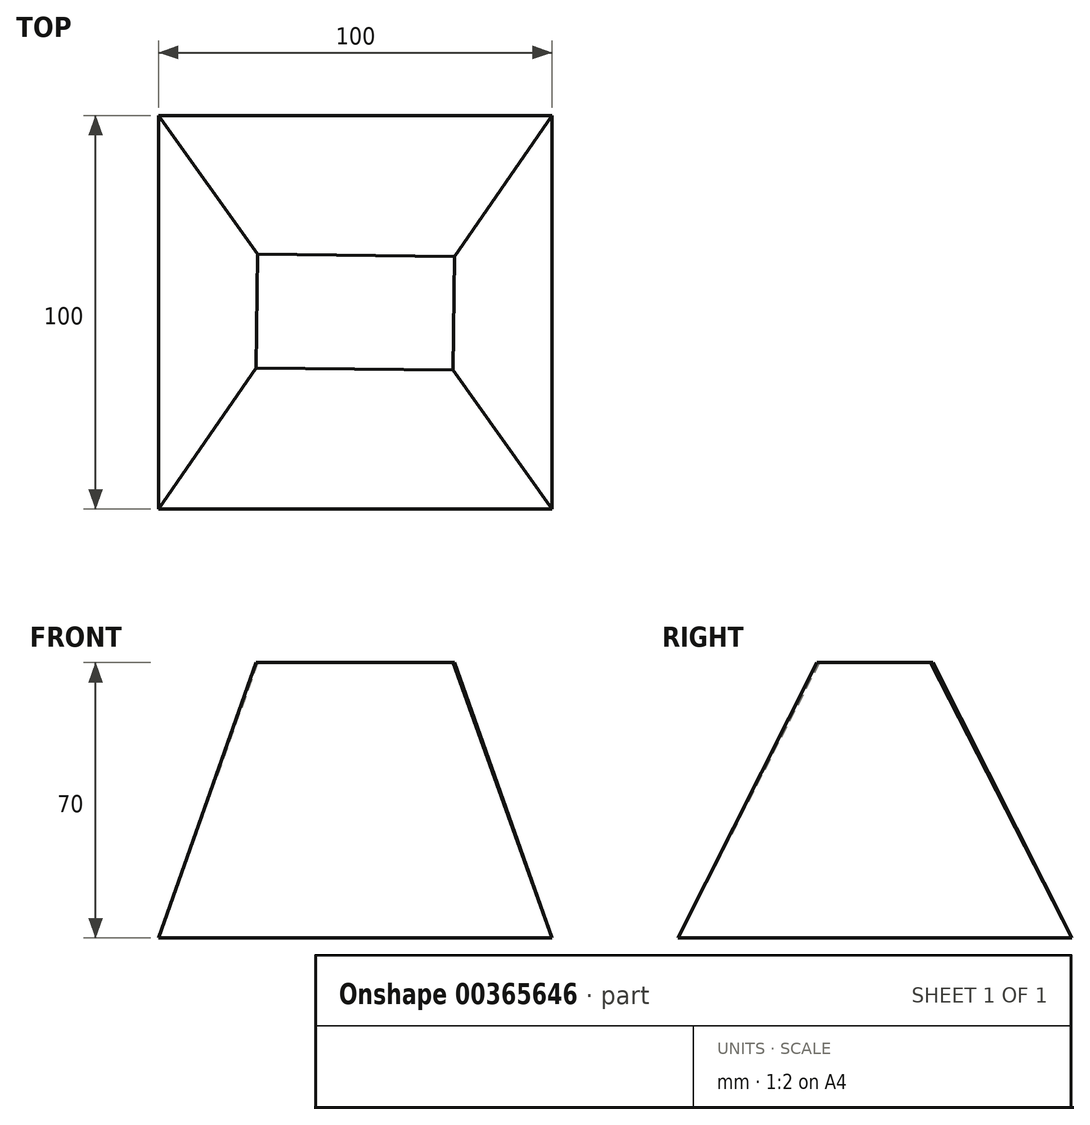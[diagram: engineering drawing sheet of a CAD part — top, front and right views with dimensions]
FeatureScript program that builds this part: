
annotation { "Feature Type Name" : "Feature", "Feature Type Description" : "" }
export const myFeature = defineFeature(function(context is Context, id is Id, definition is map)
    precondition{}
    {
        {
            var Q0;
            Q0=qCreatedBy(makeId("Top.planeOp"),FACE);
            var sketch = newSketch(context, id + "F0", { "sketchPlane" : qUnion([Q0])});
            skLineSegment(sketch, "E0.bottom", {"start": v(50, -50) * mm, "end": v(-50, -50) * mm});
            skLineSegment(sketch, "E0.top", {"start": v(50, 50) * mm, "end": v(-50, 50) * mm});
            skLineSegment(sketch, "E0.left", {"start": v(50, -50) * mm, "end": v(50, 50) * mm});
            skLineSegment(sketch, "E0.right", {"start": v(-50, -50) * mm, "end": v(-50, 50) * mm});
            skPoint(sketch, "E0.middle", {"position": v(0, 0) * mm});
            skSolve(sketch);
        }
        {
            var Q0;
            Q0=qCreatedBy(makeId("Top.planeOp"),FACE);
            cPlane(context, id + "F1", {"entities" : qUnion([Q0]), "cplaneType" : CPlaneType.OFFSET, "offset" : 70 * mm, "width" : 150 * mm, "height" : 150 * mm});
        }
        {
            var Q0;
            Q0=qCreatedBy(id+"F1.planeOp",FACE);
            var sketch = newSketch(context, id + "F2", { "sketchPlane" : qUnion([Q0])});
            skCircle(sketch, "E1.cCircle", {"center": v(0, 0) * mm, "radius": 25 * mm, "construction": true});
            skLineSegment(sketch, "E1.0", {"start": v(-0.34, -28.87) * mm, "end": v(-25.17, -14.14) * mm});
            skLineSegment(sketch, "E1.1", {"start": v(-25.17, -14.14) * mm, "end": v(-24.83, 14.73) * mm});
            skLineSegment(sketch, "E1.2", {"start": v(-24.83, 14.73) * mm, "end": v(0.34, 28.87) * mm});
            skLineSegment(sketch, "E1.3", {"start": v(0.34, 28.87) * mm, "end": v(25.17, 14.14) * mm});
            skLineSegment(sketch, "E1.4", {"start": v(25.17, 14.14) * mm, "end": v(24.83, -14.73) * mm});
            skLineSegment(sketch, "E1.5", {"start": v(24.83, -14.73) * mm, "end": v(-0.34, -28.87) * mm});
            skPoint(sketch, "E1.0.midPoint", {"position": v(-12.76, -21.5) * mm});
            skLineSegment(sketch, "E2", {"start": v(25.17, 14.14) * mm, "end": v(-24.83, 14.73) * mm});
            skLineSegment(sketch, "E3", {"start": v(24.83, -14.73) * mm, "end": v(-25.17, -14.14) * mm});
            skSolve(sketch);
        }
        {
            var Q0;
            Q0=makeQuery(id+"F2.imprint","IMPRINT",FACE,{"disambiguationData":[TD([[makeQuery(id+"F2.imprint","IMPRINT",EDGE,{"derivedFrom":sQuery(id+"F2.wireOp",EDGE,"E1.1")}),-1.0]])]});
            var Q1;
            Q1=makeQuery(id+"F0.imprint","IMPRINT",FACE,{"disambiguationData":[TD([[makeQuery(id+"F0.imprint","IMPRINT",EDGE,{"derivedFrom":sQuery(id+"F0.wireOp",EDGE,"E0.bottom")}),-1.0]])]});
            loft(context, id + "F3", {"sheetProfilesArray" : [{ "sheetProfileEntities" : qUnion([Q0]) }, { "sheetProfileEntities" : qUnion([Q1]) }]});
        }
    });
